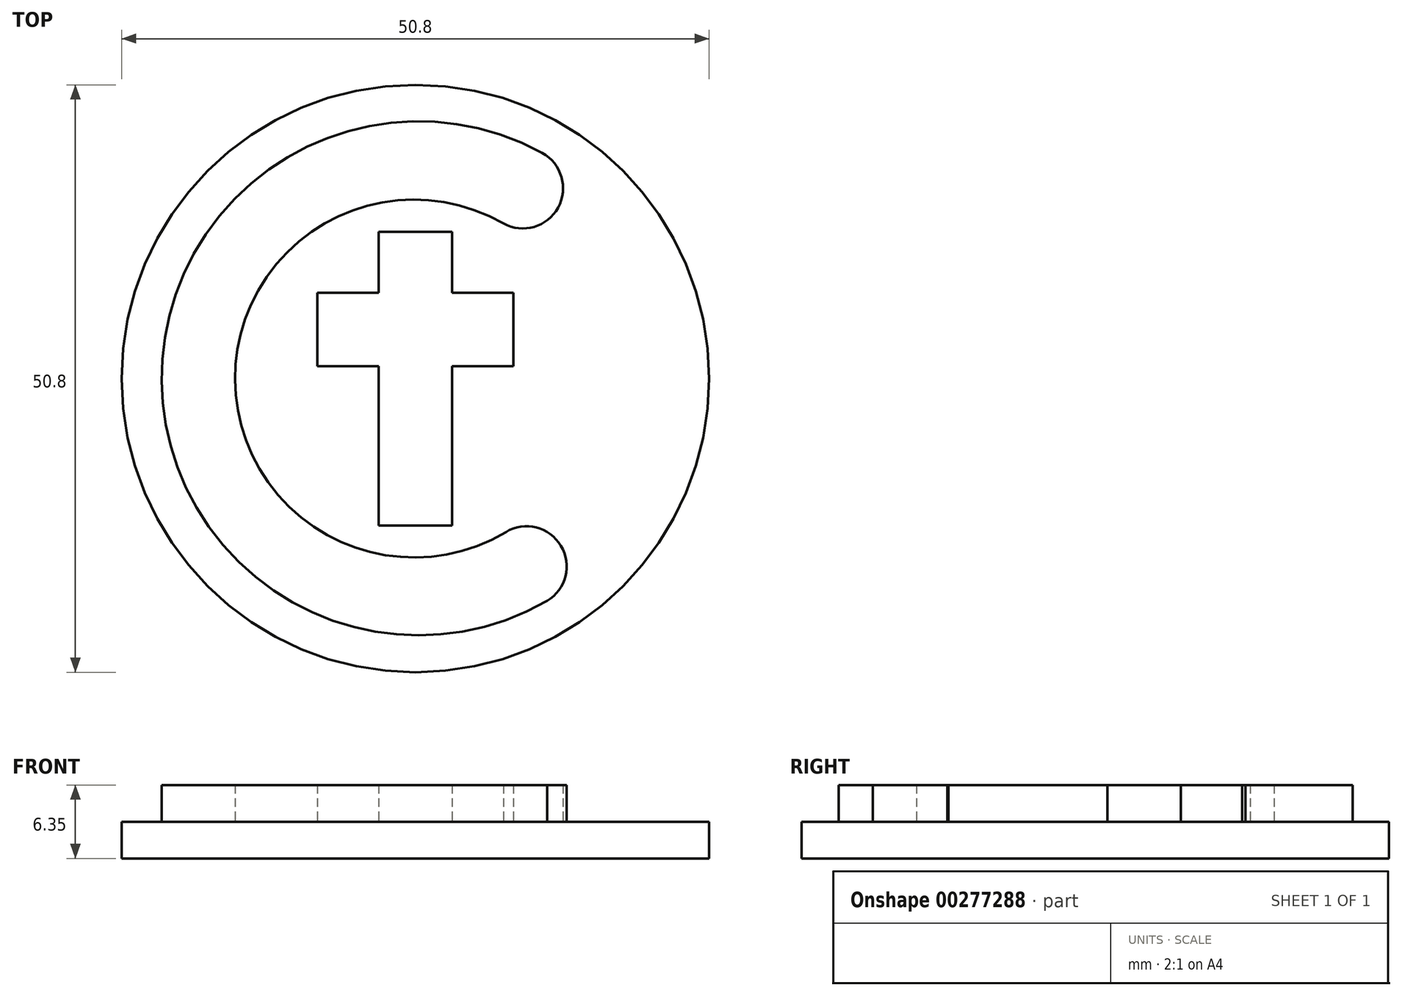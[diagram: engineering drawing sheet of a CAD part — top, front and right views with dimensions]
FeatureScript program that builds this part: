
annotation { "Feature Type Name" : "Feature", "Feature Type Description" : "" }
export const myFeature = defineFeature(function(context is Context, id is Id, definition is map)
    precondition{}
    {
        {
            var Q0;
            Q0=qCreatedBy(makeId("Top.planeOp"),FACE);
            var sketch = newSketch(context, id + "F0", { "sketchPlane" : qUnion([Q0])});
            skCircle(sketch, "E0", {"center": v(0, 0) * mm, "radius": 25.4 * mm});
            skSolve(sketch);
        }
        {
            var Q0;
            Q0 = qSketchRegion(id + "F0", true);
            extrude(context, id + "F1", {"entities" : qUnion([Q0]), "depth" : 3.17 * mm});
        }
        {
            var Q0;
            Q0=makeQuery(id+"F1.opExtrude","CAP_FACE",FACE,{"disambiguationData":[OSD([sQuery(id+"F0.wireOp",EDGE,"E0")])],"isStart":false});
            var sketch = newSketch(context, id + "F2", { "sketchPlane" : qUnion([Q0])});
            skArc(sketch, "E1.0", {"start": v(10.96, 19.5) * mm, "mid": v(-21.94, -0.23) * mm, "end": v(11.4, -19.23) * mm});
            skArc(sketch, "E2.0", {"start": v(7.62, 13.4) * mm, "mid": v(-15.6, -0.12) * mm, "end": v(7.83, -13.28) * mm});
            skArc(sketch, "E3", {"start": v(10.96, 19.5) * mm, "mid": v(12.34, 14.78) * mm, "end": v(7.62, 13.4) * mm});
            skArc(sketch, "E4", {"start": v(7.83, -13.28) * mm, "mid": v(12.59, -14.47) * mm, "end": v(11.4, -19.23) * mm});
            skLineSegment(sketch, "E5.bottom", {"start": v(-3.17, 12.7) * mm, "end": v(3.18, 12.7) * mm});
            skLineSegment(sketch, "E5.top", {"start": v(-3.18, -12.7) * mm, "end": v(3.17, -12.7) * mm});
            skLineSegment(sketch, "E5.left", {"start": v(-3.17, 12.7) * mm, "end": v(-3.18, -12.7) * mm});
            skLineSegment(sketch, "E5.right", {"start": v(3.18, 12.7) * mm, "end": v(3.17, -12.7) * mm});
            skPoint(sketch, "E5.middle", {"position": v(0, 0) * mm});
            skLineSegment(sketch, "E6", {"start": v(0, 12.7) * mm, "end": v(0, -12.7) * mm});
            skPoint(sketch, "E7", {"position": v(0, 4.23) * mm});
            skLineSegment(sketch, "E8.bottom", {"start": v(-8.47, 7.4) * mm, "end": v(8.47, 7.4) * mm});
            skLineSegment(sketch, "E8.top", {"start": v(-8.47, 1.06) * mm, "end": v(8.47, 1.06) * mm});
            skLineSegment(sketch, "E8.left", {"start": v(-8.47, 7.4) * mm, "end": v(-8.47, 1.06) * mm});
            skLineSegment(sketch, "E8.right", {"start": v(8.47, 7.4) * mm, "end": v(8.47, 1.06) * mm});
            skSolve(sketch);
        }
        {
            var Q0;
            Q0=makeQuery(id+"F2.imprint","IMPRINT",FACE,{"disambiguationData":[TD([[makeQuery(id+"F2.imprint","IMPRINT",EDGE,{"derivedFrom":sQuery(id+"F2.wireOp",EDGE,"E1.0")}),1.0]])]});
            var Q1;
            {var subQ0=sQuery(id+"F2.wireOp",EDGE,"E5.left");var subQ1=sQuery(id+"F2.wireOp",EDGE,"E5.bottom");var subQ2=makeQuery(id+"F2.imprint","INTERSECT",VERTEX,{"derivedFrom":[subQ1,subQ0]});Q1=makeQuery(id+"F2.imprint","IMPRINT",FACE,{"disambiguationData":[TD([[makeQuery(id+"F2.imprint","IMPRINT",EDGE,{"disambiguationData":[TD([[subQ2,-1.0]])],"derivedFrom":subQ1}),-1.0]])]});}
            var Q2;
            {var subQ0=sQuery(id+"F2.wireOp",EDGE,"E5.right");var subQ1=sQuery(id+"F2.wireOp",EDGE,"E5.bottom");var subQ2=makeQuery(id+"F2.imprint","INTERSECT",VERTEX,{"derivedFrom":[subQ1,subQ0]});Q2=makeQuery(id+"F2.imprint","IMPRINT",FACE,{"disambiguationData":[TD([[makeQuery(id+"F2.imprint","IMPRINT",EDGE,{"disambiguationData":[TD([[subQ2,1.0]])],"derivedFrom":subQ1}),-1.0]])]});}
            var Q3;
            {var subQ0=sQuery(id+"F2.wireOp",EDGE,"E8.bottom");var subQ1=sQuery(id+"F2.wireOp",EDGE,"E5.right");var subQ2=makeQuery(id+"F2.imprint","INTERSECT",VERTEX,{"derivedFrom":[subQ1,subQ0]});Q3=makeQuery(id+"F2.imprint","IMPRINT",FACE,{"disambiguationData":[TD([[makeQuery(id+"F2.imprint","IMPRINT",EDGE,{"disambiguationData":[TD([[subQ2,-1.0]])],"derivedFrom":subQ1}),-1.0]])]});}
            var Q4;
            {var subQ5=sQuery(id+"F2.wireOp",EDGE,"E8.right");Q4=makeQuery(id+"F2.imprint","IMPRINT",FACE,{"disambiguationData":[TD([[makeQuery(id+"F2.imprint","IMPRINT",EDGE,{"derivedFrom":subQ5}),-1.0]])]});}
            var Q5;
            {var subQ0=sQuery(id+"F2.wireOp",EDGE,"E8.bottom");var subQ1=sQuery(id+"F2.wireOp",EDGE,"E5.left");var subQ2=makeQuery(id+"F2.imprint","INTERSECT",VERTEX,{"derivedFrom":[subQ1,subQ0]});Q5=makeQuery(id+"F2.imprint","IMPRINT",FACE,{"disambiguationData":[TD([[makeQuery(id+"F2.imprint","IMPRINT",EDGE,{"disambiguationData":[TD([[subQ2,-1.0]])],"derivedFrom":subQ1}),1.0]])]});}
            var Q6;
            {var subQ5=sQuery(id+"F2.wireOp",EDGE,"E8.left");Q6=makeQuery(id+"F2.imprint","IMPRINT",FACE,{"disambiguationData":[TD([[makeQuery(id+"F2.imprint","IMPRINT",EDGE,{"derivedFrom":subQ5}),1.0]])]});}
            var Q7;
            {var subQ0=sQuery(id+"F2.wireOp",EDGE,"E5.left");var subQ1=sQuery(id+"F2.wireOp",EDGE,"E5.top");var subQ2=makeQuery(id+"F2.imprint","INTERSECT",VERTEX,{"derivedFrom":[subQ1,subQ0]});Q7=makeQuery(id+"F2.imprint","IMPRINT",FACE,{"disambiguationData":[TD([[makeQuery(id+"F2.imprint","IMPRINT",EDGE,{"disambiguationData":[TD([[subQ2,-1.0]])],"derivedFrom":subQ1}),1.0]])]});}
            var Q8;
            {var subQ0=sQuery(id+"F2.wireOp",EDGE,"E5.right");var subQ1=sQuery(id+"F2.wireOp",EDGE,"E5.top");var subQ2=makeQuery(id+"F2.imprint","INTERSECT",VERTEX,{"derivedFrom":[subQ1,subQ0]});Q8=makeQuery(id+"F2.imprint","IMPRINT",FACE,{"disambiguationData":[TD([[makeQuery(id+"F2.imprint","IMPRINT",EDGE,{"disambiguationData":[TD([[subQ2,1.0]])],"derivedFrom":subQ1}),1.0]])]});}
            extrude(context, id + "F3", {"entities" : qUnion([Q0, Q1, Q2, Q3, Q4, Q5, Q6, Q7, Q8]), "operationType" : NewBodyOperationType.ADD, "depth" : 3.17 * mm});
        }
    });
